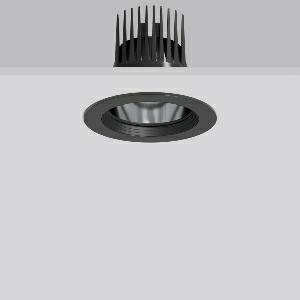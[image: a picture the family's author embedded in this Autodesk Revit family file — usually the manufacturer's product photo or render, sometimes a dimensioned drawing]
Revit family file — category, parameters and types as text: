
# Revit family: heledon_maxi_e_901773_003_76_9c9a
name_source: partatom
category: Lighting Fixtures
units: mm (PartAtom-declared; Revit-internal decimal feet)

## family parameters
Cut with Voids When Loaded = No
Host = Face
Light Source = No
Part Type = Normal
Room Calculation Point = No
Round Connector Dimension = Use Diameter
Shared = No

## types (1)
- HELEDON maxi E (1 x LED Modul 932 fresh meat, 2050 lm, 3200)
    Apparent Load = 33 VA
    Approval mark = CE
    CIE Flux Codes = 96 100 100 100 100
    Color Rendering = 90
    Color Temperature = 3200
    Default Elevation = 1800 mm
    Description = Series: HELEDON maxi
Round recessed downlight. Housing: die-cast aluminium, powder-coated. Black plastic ring and recessed LED to prevent glare from the side. Optical assembly with reflector made of MIRO-Silver with 98% total light reflection for outstanding efficiency - can be changed without tools. Special LED for illumination of meat included. Suitable for Recessed ceiling mounting. Installation without tools thanks to spring fastening system. Including separate LED converter with connecting cable 600 mm.High quality converter without flickering and stroboscopic effect. Through-wiring box (5 pole) available as accessory. The following accessories can be mounted without use of tools: interchangeable lenses, decorative glasses, honeycomb louvre, clear and frosted diffusers, white interchangeable plastic ring. 
Colour: deep black, matt (RAL 9005)
Diameter: 162 mm
Height: 3 mm
Cut-out diameter: 152 mm
Recess height: 200 mm
Luminaire: recess height: 135 mm
Lamp: LED
Socket: without socket
Colour temperature: fresh meat
System power: 33 W
Rated luminous flux: 2050 lm
Luminous efficiency: 62 lm/W
Control gear: Converter, dimmable, DALI
Protection class: II
Type of protection: IP 20
    Height = 0 mm  [stored 0 ft]
    Lamp = 1 x LED Modul 932 fresh meat
    Lamp Light Flux = 2050 lm
    Lamp count = 1
    Length = 162 mm
    Lifetime = 50000 h
    Luminous efficacy = 62 lm/W
    Manufacturer = RZB
    ModVariant = No
    Model = 901773.003.76
    Mounting Place = Ceiling
    Mounting Type = Recessed
    Number of Poles = 1
    OnlyDefault = Yes
    Power Factor = 1
    Product Name = HELEDON maxi E
    Product group = Recessed downlights
    ProductGroupID = 402
    Protection Class = Protection class II
    Protection Degree = IP 20
    RLX_Detail_Level = 1
    RLX_Emergency_Light_Flux = 0 lm
    RLX_Emergency_Type = 0
    RLX_Emergency_Type_DB = No
    RlxData = <blob elided: 122341 chars, md5=182f76e0>
    Socket = socket
    Standby Power = 0 W
    System Light Flux = 2050 lm
    System Power = 33 W
    Type Comments = Product without accessories
    Type Image = 901662.003.jpg
    URL = http://relux.com
    VarID = ---
    Voltage = 230 V
    Voltage Range = 220-240 V
    Weight = 0.00 kg
    Width = 0 mm  [stored 0 ft]

note: [stored X ft] marks values corroborated as IEEE doubles in the binary element streams (Revit-internal decimal feet)

## geometry (parser evidence)
native form markers: Blend x4, Sweep x12
no freeform markers — native parametric forms only
